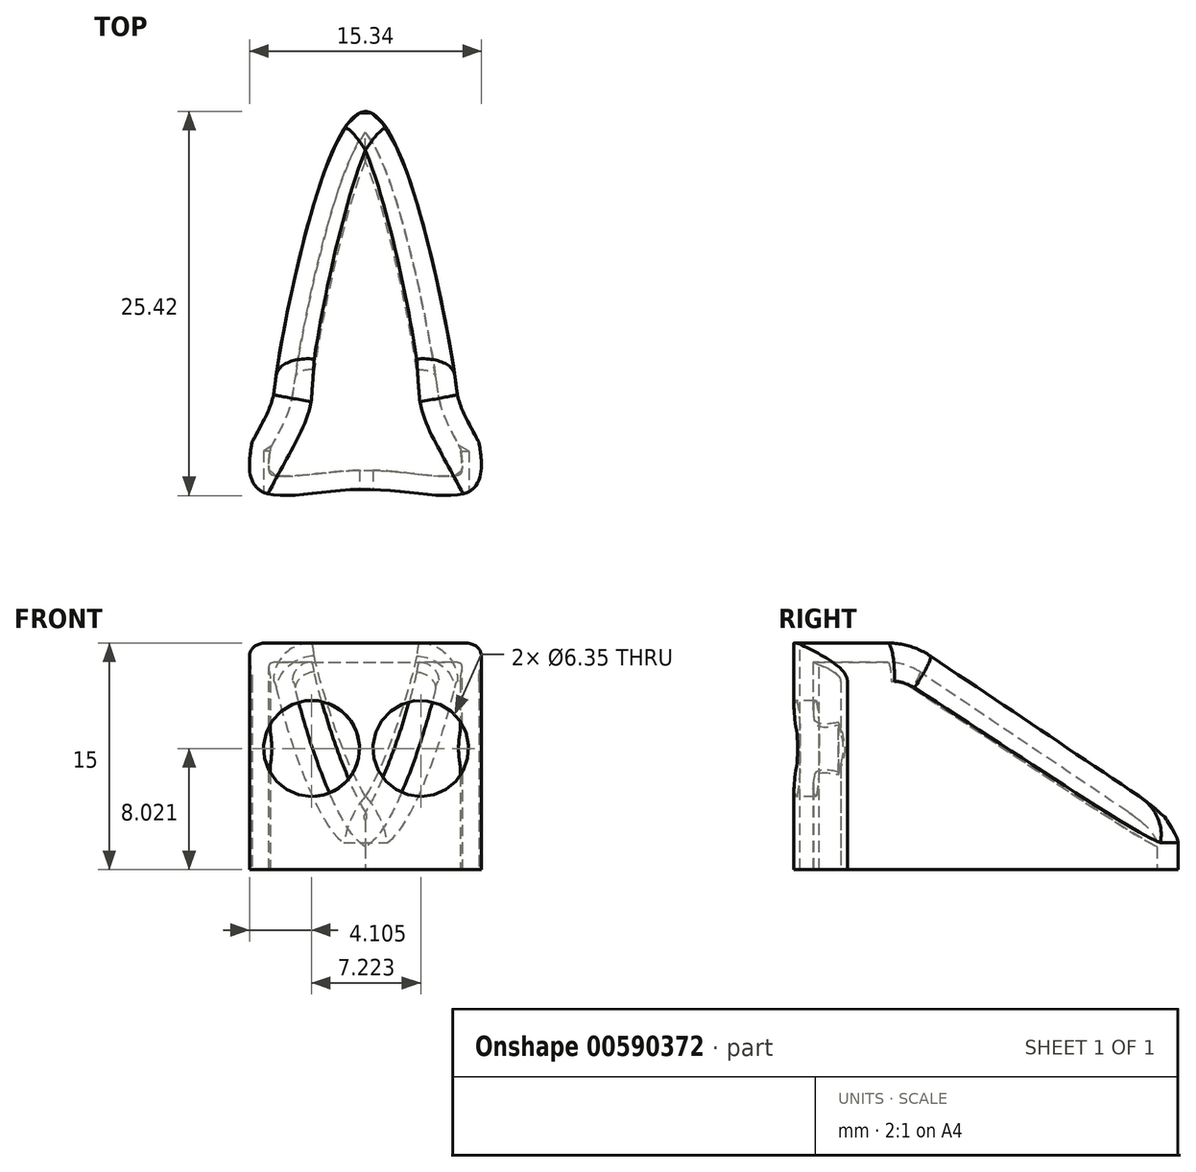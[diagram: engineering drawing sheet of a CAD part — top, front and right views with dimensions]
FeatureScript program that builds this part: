
annotation { "Feature Type Name" : "Feature", "Feature Type Description" : "" }
export const myFeature = defineFeature(function(context is Context, id is Id, definition is map)
    precondition{}
    {
        {
            assignVariable(context, id + "F0", {"name" : "bridge2tip", "anyValue" : 25 * mm});
        }
        {
            assignVariable(context, id + "F1", {"name" : "lengthofnose", "anyValue" : 15 * mm});
        }
        {
            var Q0;
            Q0=qCreatedBy(makeId("Top.planeOp"),FACE);
            var sketch = newSketch(context, id + "F2", { "sketchPlane" : qUnion([Q0])});
            skCircle(sketch, "E0", {"center": v(0, 0) * mm, "radius": 7.5 * mm});
            skSolve(sketch);
        }
        {
            var Q0;
            Q0=qCreatedBy(makeId("Front.planeOp"),FACE);
            cPlane(context, id + "F3", {"entities" : qUnion([Q0]), "cplaneType" : CPlaneType.OFFSET, "offset" : (getVariable(context, 'bridge2tip') - getVariable(context, 'lengthofnose')) / 3, "width" : 152.4 * mm, "height" : 152.4 * mm});
        }
        {
            var Q0;
            Q0=qCreatedBy(id+"F3.planeOp",FACE);
            cPlane(context, id + "F4", {"entities" : qUnion([Q0]), "cplaneType" : CPlaneType.OFFSET, "offset" : (getVariable(context, 'bridge2tip') - getVariable(context, 'lengthofnose')) * 4 / 5, "oppositeDirection" : true, "width" : 152.4 * mm, "height" : 152.4 * mm});
        }
        {
            var Q0;
            Q0=qCreatedBy(makeId("Top.planeOp"),FACE);
            var sketch = newSketch(context, id + "F5", { "sketchPlane" : qUnion([Q0])});
            skFitSpline(sketch, "E1", {"points": [v(-7.5, 0) * mm, v(-5.87, 4.67) * mm, v(0, 21.88) * mm, v(5.87, 4.67) * mm, v(7.5, 0) * mm], "startDerivative": vector(27.13, 50) * mm, "endDerivative": vector(27.15, -50) * mm});
            skFitSpline(sketch, "E2", {"points": [v(-7.5, 0) * mm, v(-6.72, -3.33) * mm, v(0, -3.12) * mm, v(6.72, -3.33) * mm, v(7.5, 0) * mm], "startDerivative": vector(-5.46, -27.01) * mm, "endDerivative": vector(-5.22, 26.98) * mm});
            skSolve(sketch);
        }
        {
            var Q0;
            Q0 = qSketchRegion(id + "F5", true);
            extrude(context, id + "F6", {"entities" : qUnion([Q0]), "depth" : getVariable(context, 'lengthofnose'), "offsetDistance" : 25.4 * mm});
        }
        {
            var Q0;
            Q0=qCreatedBy(makeId("Right.planeOp"),FACE);
            var sketch = newSketch(context, id + "F7", { "sketchPlane" : qUnion([Q0])});
            skLineSegment(sketch, "E3", {"start": v(26.53, 0) * mm, "end": v(0, 17.83) * mm});
            skLineSegment(sketch, "E4", {"start": v(0, 17.83) * mm, "end": v(8.43, 30.38) * mm});
            skLineSegment(sketch, "E5", {"start": v(8.43, 30.38) * mm, "end": v(34.35, 10.3) * mm});
            skLineSegment(sketch, "E6", {"start": v(34.35, 10.3) * mm, "end": v(26.53, 0) * mm});
            skSolve(sketch);
        }
        {
            var Q0;
            Q0 = qSketchRegion(id + "F7", true);
            extrude(context, id + "F8", {"entities" : qUnion([Q0]), "operationType" : NewBodyOperationType.REMOVE, "endBound" : BoundingType.SYMMETRIC, "oppositeDirection" : true, "depth" : 25.4 * mm, "offsetDistance" : 25.4 * mm});
        }
        {
            var Q0;
            Q0=makeQuery(id+"F8.boolean.opBoolean","INTERSECT",EDGE,{"derivedFrom":[makeQuery(id+"F6.opExtrude","CAP_FACE",FACE,{"disambiguationData":[OSD([sQuery(id+"F5.wireOp",EDGE,"E1"),sQuery(id+"F5.wireOp",EDGE,"E2")])],"isStart":false}),makeQuery(id+"F8.opExtrude","SWEPT_FACE",FACE,{"disambiguationData":[OSD([sQuery(id+"F7.wireOp",EDGE,"E3")])]})]});
            fillet(context, id + "F9", {"entities" : qUnion([Q0]), "radius" : 5.08 * mm, "tangentPropagation" : true, "allowEdgeOverflow" : false});
        }
        {
            var Q0;
            Q0=makeQuery(id+"F8.boolean.opBoolean","INTERSECT",EDGE,{"derivedFrom":[makeQuery(id+"F6.opExtrude","SWEPT_FACE",FACE,{"disambiguationData":[OSD([sQuery(id+"F5.wireOp",EDGE,"E1")])]}),makeQuery(id+"F8.opExtrude","SWEPT_FACE",FACE,{"disambiguationData":[OSD([sQuery(id+"F7.wireOp",EDGE,"E3")])]})]});
            fillet(context, id + "F10", {"entities" : qUnion([Q0]), "radius" : 2.54 * mm, "tangentPropagation" : true, "allowEdgeOverflow" : false});
        }
        {
            var Q0;
            Q0=makeQuery(id+"F6.opExtrude","CAP_FACE",FACE,{"disambiguationData":[OSD([sQuery(id+"F5.wireOp",EDGE,"E1"),sQuery(id+"F5.wireOp",EDGE,"E2")])],"isStart":true});
            shell(context, id + "F11", {"entities" : qUnion([Q0]), "thickness" : 1.27 * mm});
        }
        {
            var Q0;
            Q0=qCreatedBy(makeId("Front.planeOp"),FACE);
            cPlane(context, id + "F12", {"entities" : qUnion([Q0]), "cplaneType" : CPlaneType.OFFSET, "offset" : 4.32 * mm, "width" : 152.4 * mm, "height" : 152.4 * mm});
        }
        {
            var Q0;
            Q0=qCreatedBy(id+"F12.planeOp",FACE);
            var sketch = newSketch(context, id + "F13", { "sketchPlane" : qUnion([Q0])});
            skPoint(sketch, "E7", {"position": v(3.66, 8.02) * mm});
            skPoint(sketch, "E8", {"position": v(-3.57, 8.02) * mm});
            skSolve(sketch);
        }
        {
            var Q0;
            Q0=sQuery(id+"F13.wireOp",VERTEX,"E7");
            var Q1;
            Q1=sQuery(id+"F13.wireOp",VERTEX,"E8");
            var Q2;
            Q2=makeQuery(id+"F6.opExtrude","SWEPT_BODY",BODY,{"disambiguationData":[OSD([sQuery(id+"F5.wireOp",EDGE,"E1"),sQuery(id+"F5.wireOp",EDGE,"E2")])]});
            hole(context, id + "F14", {"style" : HoleStyle.SIMPLE, "endStyle" : HoleEndStyle.BLIND, "holeDiameter" : 6.35 * mm, "majorDiameter" : 6.35 * mm, "holeDepth" : 2.54 * mm, "isTappedThrough" : true, "tappedDepth" : 12.7 * mm, "tapClearance" : 3, "locations" : qUnion([Q0, Q1]), "scope" : qUnion([Q2])});
        }
    });
